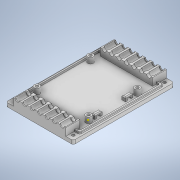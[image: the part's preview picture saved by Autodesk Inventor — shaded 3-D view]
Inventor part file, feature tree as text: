
AUTODESK INVENTOR PART (.ipt)
format: ipt  version: 2021 (Build 250183000, 183)  size: 581,120 bytes
history: native  units: mm
features: extrude x17, sketch x17, fillet x6
ambient origin geometry x8: Origin, YZ Plane, XZ Plane, XY Plane, X Axis, Y Axis, Z Axis, Center Point
bodies: Solid1 (feature_tree)
feature tree (40):
  extrude  "Extrusion1"  Depth=62.0mm
  extrude  "Extrusion2"  Depth=3.0mm
  extrude  "Extrusion3"  Depth=3.0mm
  extrude  "Extrusion4"  Depth=3.0mm
  fillet  "Fillet1"  Radius=6.0mm
  fillet  "Fillet2"  Radius=3.0mm
  fillet  "Fillet3"  Radius=57.4mm
  extrude  "Extrusion7"  Depth=0.8mm
  extrude  "Extrusion8"  Depth=4.8mm
  extrude  "Extrusion9"  Depth=6.0mm
  extrude  "Extrusion10"  Depth=20.0mm
  extrude  "Extrusion11"  Depth=1.0mm
  extrude  "Extrusion12"  Depth=2.0mm TaperAngle=0.0deg
  extrude  "Extrusion13"  TaperAngle=0.0deg  [1 undecoded]
  fillet  "Fillet8"  [1 undecoded]
  fillet  "Fillet9"  Radius=6.0mm
  extrude  "Extrusion14"  TaperAngle=0.0deg  [1 undecoded]
  extrude  "Extrusion15"  Depth=2.0mm
  extrude  "Extrusion16"  Depth=4.0mm
  extrude  "Extrusion17"  Depth=4.0mm
  fillet  "Fillet11"  Radius=2.0mm
  extrude  "Extrusion18"  Depth=2.0mm
  extrude  "Extrusion19"  Depth=35.0mm
  sketch  "Sketch25"  dims[d75=2.0mm d76=35.0mm d77=8.0mm d78=0.0mm d79=4.0mm d80=0.0mm d81=1.0mm d82=1.0mm d83=1.0mm d122=15.0mm d123=15.0mm d124=56.0mm d125=4.0mm d126=12.0mm d127=56.0mm d128=4.0mm d129=12.0mm d130=8.0mm d131=0.0mm d132=6.0mm d133=4.0mm d134=70.0mm d136=8.0mm d137=10.0mm d139=10.0mm d141=11.0mm d142=0.0mm d143=6.2mm d144=4.0mm d145=70.0mm d147=8.0mm d148=10.0mm d150=10.0mm d152=11.0mm d153=0.0mm d158=1.0mm d159=1.0mm d160=8.0mm d161=2.0mm d162=0.0mm d163=0.0mm d164=0.0mm d165=4.0mm d166=4.0mm d167=0.0mm d168=2.0mm d169=0.0mm d177=2.0mm d178=2.0mm d179=8.0mm d180=0.0mm d181=2.0mm d182=2.0mm d184=2.0mm d186=2.0mm d187=8.0mm d190=8.0mm d193=8.0mm d196=8.0mm d199=2.0mm d200=2.0mm d201=2.0mm d202=2.0mm d203=2.0mm d204=0.0mm d205=0.5mm d206=0.5mm d211=10.0mm d212=0.0mm d213=2.0mm d214=0.0mm d215=8.0mm d216=5.0mm d217=5.0mm d218=3.0mm d219=8.0mm d220=8.0mm d221=8.0mm d222=5.0mm d223=5.0mm d224=5.0mm d225=5.0mm d226=3.0mm d227=3.0mm d228=3.0mm d229=10.0mm d230=0.0mm d231=7.0mm d232=7.0mm d233=7.0mm d234=7.0mm d235=2.0mm d236=0.0mm d237=2.0mm d238=4.5mm d239=4.0mm d240=70.0mm d242=8.0mm d243=10.0mm d245=10.0mm d247=20.0mm d248=0.0mm d249=4.0mm d250=4.5mm d251=70.0mm d253=8.0mm d254=10.0mm d256=10.0mm d258=20.0mm d259=0.0mm d260=5.0mm d261=5.0mm]
  sketch  "Sketch2"  dims[d14=66.0mm d15=62.0mm]
  sketch  "Sketch4"  dims[d16=3.0mm d17=3.0mm]
  sketch  "Sketch5"  dims[d18=3.0mm d19=3.0mm]
  sketch  "Sketch6"  dims[d20=3.0mm d21=4.5mm d22=6.0mm d23=3.0mm d24=57.4mm]
  sketch  "Sketch10"  dims[d25=54.35mm d26=0.8mm]
  sketch  "Sketch11"  dims[d27=51.56mm d28=4.8mm]
  sketch  "Sketch12"  dims[d29=6.0mm d30=6.0mm]
  sketch  "Sketch13"  dims[d31=6.0mm d32=20.0mm]
  sketch  "Sketch14"  dims[d33=20.0mm d34=1.0mm]
  sketch  "Sketch17"  dims[d35=1.0mm d36=2.0mm d37=0.0mm]
  sketch  "Sketch19"  dims[d38=66.0mm d39=62.0mm d40=3.0mm d41=3.0mm d42=3.0mm d43=3.0mm d44=3.0mm d45=4.5mm d46=6.0mm d47=3.0mm d48=57.4mm d49=54.35mm d50=0.8mm d51=51.56mm d52=4.8mm d53=6.0mm d54=6.0mm d55=6.0mm d56=20.0mm d57=20.0mm d58=1.0mm d59=1.0mm d60=0.0mm d61=0.0mm d62=6.0mm d63=0.0mm]
  sketch  "Sketch20"  dims[d64=2.0mm d65=0.0mm]
  sketch  "Sketch21"  dims[d66=2.0mm d67=2.0mm]
  sketch  "Sketch22"  dims[d68=30.0mm d69=4.0mm]
  sketch  "Sketch23"  dims[d70=4.0mm d71=4.0mm d72=2.0mm]
  sketch  "Sketch24"  dims[d73=2.0mm d74=2.0mm]
note: 3 required parameter values undecoded (feature->parameter linkage not recoverable at this tier; creation-order binding heuristic only, values carry confidence <= 0.55)
